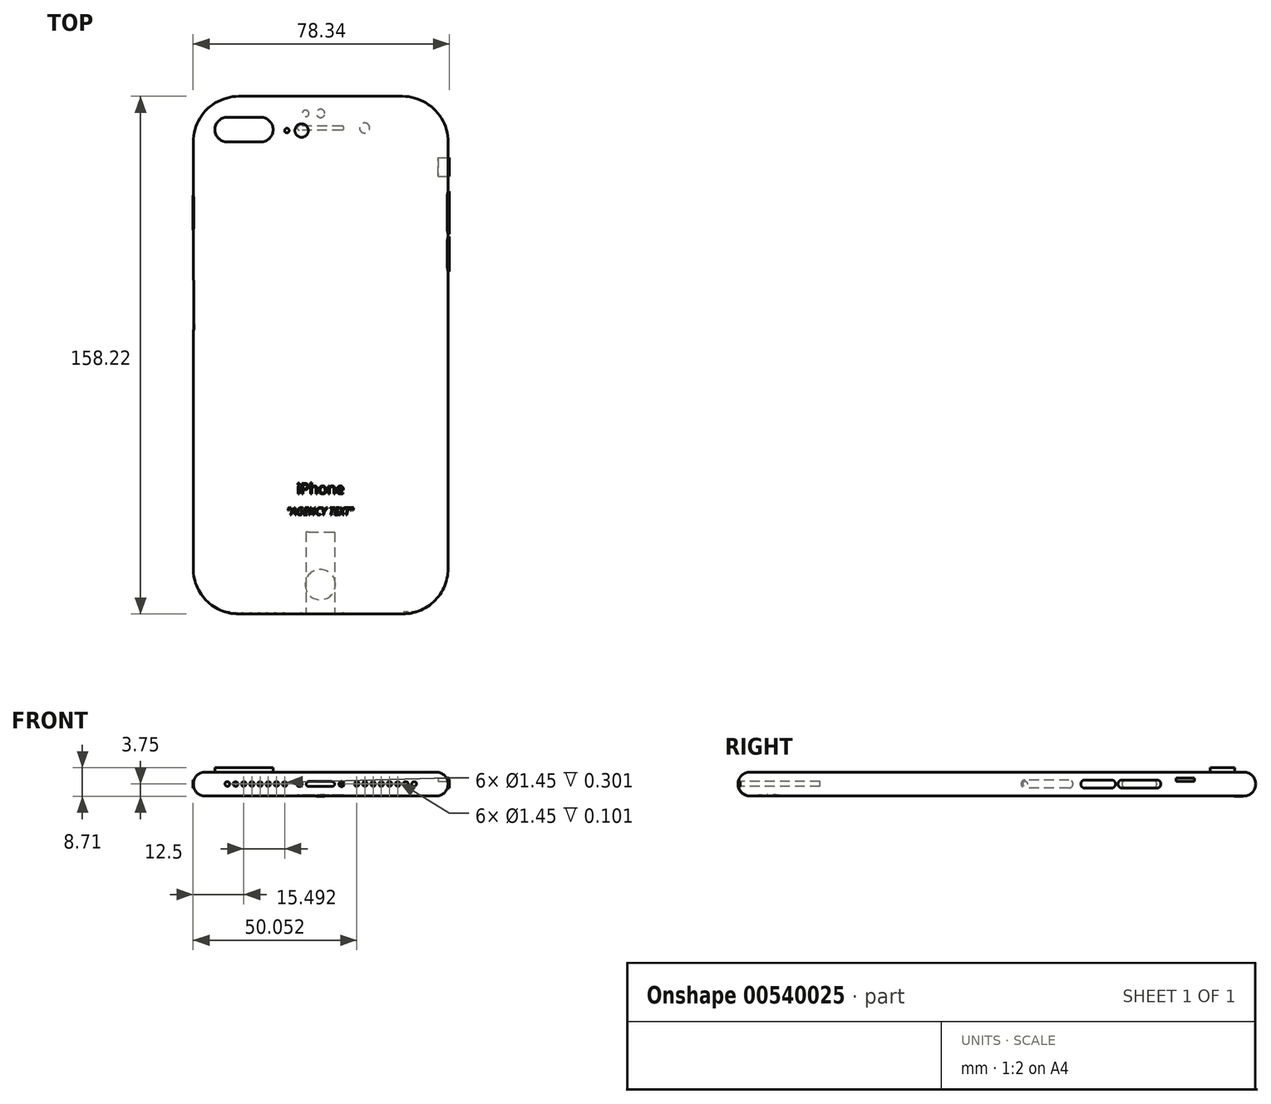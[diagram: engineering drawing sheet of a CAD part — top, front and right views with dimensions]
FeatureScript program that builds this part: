
annotation { "Feature Type Name" : "Feature", "Feature Type Description" : "" }
export const myFeature = defineFeature(function(context is Context, id is Id, definition is map)
    precondition{}
    {
        {
            var Q0;
            Q0=qCreatedBy(makeId("Top.planeOp"),FACE);
            var sketch = newSketch(context, id + "F0", { "sketchPlane" : qUnion([Q0])});
            skLineSegment(sketch, "E0.bottom", {"start": v(-14.7, 124.28) * mm, "end": v(35.32, 124.28) * mm});
            skLineSegment(sketch, "E0.top", {"start": v(-14.7, -33.94) * mm, "end": v(35.32, -33.94) * mm});
            skLineSegment(sketch, "E0.left", {"start": v(-28.64, 110.34) * mm, "end": v(-28.64, -20) * mm});
            skLineSegment(sketch, "E0.right", {"start": v(49.26, 110.34) * mm, "end": v(49.26, -20) * mm});
            skPoint(sketch, "E1.visualSharp", {"position": v(49.26, -33.94) * mm});
            skArc(sketch, "E1.filletArc", {"start": v(35.32, -33.94) * mm, "mid": v(45.18, -29.86) * mm, "end": v(49.26, -20) * mm});
            skPoint(sketch, "E2.visualSharp", {"position": v(-28.64, -33.94) * mm});
            skArc(sketch, "E2.filletArc", {"start": v(-28.64, -20) * mm, "mid": v(-24.55, -29.86) * mm, "end": v(-14.7, -33.94) * mm});
            skPoint(sketch, "E3.visualSharp", {"position": v(49.26, 124.28) * mm});
            skArc(sketch, "E3.filletArc", {"start": v(49.26, 110.34) * mm, "mid": v(45.18, 120.2) * mm, "end": v(35.32, 124.28) * mm});
            skPoint(sketch, "E4.visualSharp", {"position": v(-28.64, 124.28) * mm});
            skArc(sketch, "E4.filletArc", {"start": v(-14.7, 124.28) * mm, "mid": v(-24.55, 120.2) * mm, "end": v(-28.64, 110.34) * mm});
            skSolve(sketch);
        }
        {
            var Q0;
            Q0 = qSketchRegion(id + "F0", true);
            extrude(context, id + "F1", {"entities" : qUnion([Q0]), "depth" : 7.3 * mm, "offsetDistance" : 25 * mm});
        }
        {
            var Q0;
            Q0=makeQuery(id+"F1.opExtrude","CAP_EDGE",EDGE,{"disambiguationData":[OSD([sQuery(id+"F0.wireOp",EDGE,"E0.right")])],"isStart":true});
            fillet(context, id + "F2", {"entities" : qUnion([Q0]), "radius" : 3.65 * mm, "tangentPropagation" : true, "allowEdgeOverflow" : false});
        }
        {
            var Q0;
            Q0=makeQuery(id+"F1.opExtrude","CAP_EDGE",EDGE,{"disambiguationData":[OSD([sQuery(id+"F0.wireOp",EDGE,"E0.right")])],"isStart":false});
            fillet(context, id + "F3", {"entities" : qUnion([Q0]), "radius" : 3.65 * mm, "tangentPropagation" : true, "allowEdgeOverflow" : false});
        }
        {
            var Q0;
            Q0=makeQuery(id+"F1.opExtrude","CAP_FACE",FACE,{"disambiguationData":[OSD([sQuery(id+"F0.wireOp",EDGE,"E0.bottom"),sQuery(id+"F0.wireOp",EDGE,"E0.top"),sQuery(id+"F0.wireOp",EDGE,"E0.left"),sQuery(id+"F0.wireOp",EDGE,"E0.right"),sQuery(id+"F0.wireOp",EDGE,"E1.filletArc"),sQuery(id+"F0.wireOp",EDGE,"E2.filletArc"),sQuery(id+"F0.wireOp",EDGE,"E3.filletArc"),sQuery(id+"F0.wireOp",EDGE,"E4.filletArc")])],"isStart":false});
            var sketch = newSketch(context, id + "F4", { "sketchPlane" : qUnion([Q0])});
            skLineSegment(sketch, "E5.bottom", {"start": v(-14.75, 124.28) * mm, "end": v(35.27, 124.28) * mm});
            skLineSegment(sketch, "E5.top", {"start": v(-14.75, -33.92) * mm, "end": v(35.27, -33.92) * mm});
            skLineSegment(sketch, "E5.left", {"start": v(-28.69, 110.34) * mm, "end": v(-28.69, -19.98) * mm});
            skLineSegment(sketch, "E5.right", {"start": v(49.21, 110.34) * mm, "end": v(49.21, -19.98) * mm});
            skPoint(sketch, "E6.visualSharp", {"position": v(49.21, -33.92) * mm});
            skArc(sketch, "E6.filletArc", {"start": v(35.27, -33.92) * mm, "mid": v(45.13, -29.84) * mm, "end": v(49.21, -19.98) * mm});
            skPoint(sketch, "E7.visualSharp", {"position": v(-28.69, -33.92) * mm});
            skArc(sketch, "E7.filletArc", {"start": v(-28.69, -19.98) * mm, "mid": v(-24.6, -29.84) * mm, "end": v(-14.75, -33.92) * mm});
            skPoint(sketch, "E8.visualSharp", {"position": v(49.21, 124.28) * mm});
            skArc(sketch, "E8.filletArc", {"start": v(49.21, 110.34) * mm, "mid": v(45.13, 120.2) * mm, "end": v(35.27, 124.28) * mm});
            skPoint(sketch, "E9.visualSharp", {"position": v(-28.69, 124.28) * mm});
            skArc(sketch, "E9.filletArc", {"start": v(-14.75, 124.28) * mm, "mid": v(-24.6, 120.2) * mm, "end": v(-28.69, 110.34) * mm});
            skText(sketch, "E10", { "text": "iPhone", "fontName": "OpenSans-Regular.ttf"});
            skText(sketch, "E11", { "text": "\"AGENCY TEXT\"", "fontName": "OpenSans-Italic.ttf"});
            skCircle(sketch, "E12", {"center": v(4.5, 113.8) * mm, "radius": 2.05 * mm});
            skCircle(sketch, "E13", {"center": v(0, 113.8) * mm, "radius": 0.7 * mm});
            skLineSegment(sketch, "E14.bottom", {"start": v(-7.97, 117.88) * mm, "end": v(-18.24, 117.88) * mm});
            skLineSegment(sketch, "E14.top", {"start": v(-7.97, 110.34) * mm, "end": v(-18.24, 110.34) * mm});
            skLineSegment(sketch, "E14.left", {"start": v(-4.2, 114.1) * mm, "end": v(-4.2, 114.1) * mm});
            skLineSegment(sketch, "E14.right", {"start": v(-22, 114.1) * mm, "end": v(-22, 114.1) * mm});
            skPoint(sketch, "E15.visualSharp", {"position": v(-22, 117.88) * mm});
            skArc(sketch, "E15.filletArc", {"start": v(-18.24, 117.88) * mm, "mid": v(-20.9, 116.77) * mm, "end": v(-22, 114.1) * mm});
            skPoint(sketch, "E16.visualSharp", {"position": v(-22, 110.34) * mm});
            skArc(sketch, "E16.filletArc", {"start": v(-22, 114.1) * mm, "mid": v(-20.9, 111.44) * mm, "end": v(-18.24, 110.34) * mm});
            skPoint(sketch, "E17.visualSharp", {"position": v(-4.2, 110.34) * mm});
            skArc(sketch, "E17.filletArc", {"start": v(-7.97, 110.34) * mm, "mid": v(-5.3, 111.44) * mm, "end": v(-4.2, 114.1) * mm});
            skPoint(sketch, "E18.visualSharp", {"position": v(-4.2, 117.88) * mm});
            skArc(sketch, "E18.filletArc", {"start": v(-4.2, 114.1) * mm, "mid": v(-5.3, 116.77) * mm, "end": v(-7.97, 117.88) * mm});
            const initialGuessF4  = {"E10": [0.003, 0.00278, 1, 0, 0.00322], "E11": [0, -0.00364, 1, 0, 0.00222]};
            skSetInitialGuess(sketch, initialGuessF4);
            skSolve(sketch);
        }
        {
            var Q0;
            Q0=makeQuery(id+"F4.imprint","IMPRINT",FACE,{"disambiguationData":[TD([[makeQuery(id+"F4.imprint","IMPRINT",EDGE,{"derivedFrom":sQuery(id+"F4.wireOp",EDGE,"E10.sketch_text.stroke-79")}),-1.0]])]});
            var Q1;
            Q1=makeQuery(id+"F4.imprint","IMPRINT",FACE,{"disambiguationData":[TD([[makeQuery(id+"F4.imprint","IMPRINT",EDGE,{"derivedFrom":sQuery(id+"F4.wireOp",EDGE,"E10.sketch_text.stroke-62")}),-1.0]])]});
            var Q2;
            Q2=makeQuery(id+"F4.imprint","IMPRINT",FACE,{"disambiguationData":[TD([[makeQuery(id+"F4.imprint","IMPRINT",EDGE,{"derivedFrom":sQuery(id+"F4.wireOp",EDGE,"E10.sketch_text.stroke-45")}),-1.0]])]});
            var Q3;
            Q3=makeQuery(id+"F4.imprint","IMPRINT",FACE,{"disambiguationData":[TD([[makeQuery(id+"F4.imprint","IMPRINT",EDGE,{"derivedFrom":sQuery(id+"F4.wireOp",EDGE,"E10.sketch_text.stroke-27")}),-1.0]])]});
            var Q4;
            Q4=makeQuery(id+"F4.imprint","IMPRINT",FACE,{"disambiguationData":[TD([[makeQuery(id+"F4.imprint","IMPRINT",EDGE,{"derivedFrom":sQuery(id+"F4.wireOp",EDGE,"E10.sketch_text.stroke-12")}),-1.0]])]});
            var Q5;
            Q5=makeQuery(id+"F4.imprint","IMPRINT",FACE,{"disambiguationData":[TD([[makeQuery(id+"F4.imprint","IMPRINT",EDGE,{"derivedFrom":sQuery(id+"F4.wireOp",EDGE,"E10.sketch_text.stroke-0")}),-1.0]])]});
            var Q6;
            Q6=makeQuery(id+"F4.imprint","IMPRINT",FACE,{"disambiguationData":[TD([[makeQuery(id+"F4.imprint","IMPRINT",EDGE,{"derivedFrom":sQuery(id+"F4.wireOp",EDGE,"E10.sketch_text.stroke-4")}),-1.0]])]});
            extrude(context, id + "F5", {"entities" : qUnion([Q0, Q1, Q2, Q3, Q4, Q5, Q6]), "operationType" : NewBodyOperationType.REMOVE, "oppositeDirection" : true, "depth" : .1 * mm, "offsetDistance" : 25 * mm});
        }
        {
            var Q0;
            Q0=makeQuery(id+"F4.imprint","IMPRINT",FACE,{"disambiguationData":[TD([[makeQuery(id+"F4.imprint","IMPRINT",EDGE,{"derivedFrom":sQuery(id+"F4.wireOp",EDGE,"E11.sketch_text.stroke-8")}),-1.0]])]});
            var Q1;
            Q1=makeQuery(id+"F4.imprint","IMPRINT",FACE,{"disambiguationData":[TD([[makeQuery(id+"F4.imprint","IMPRINT",EDGE,{"derivedFrom":sQuery(id+"F4.wireOp",EDGE,"E11.sketch_text.stroke-4")}),-1.0]])]});
            var Q2;
            Q2=makeQuery(id+"F4.imprint","IMPRINT",FACE,{"disambiguationData":[TD([[makeQuery(id+"F4.imprint","IMPRINT",EDGE,{"derivedFrom":sQuery(id+"F4.wireOp",EDGE,"E11.sketch_text.stroke-0")}),-1.0]])]});
            var Q3;
            Q3=makeQuery(id+"F4.imprint","IMPRINT",FACE,{"disambiguationData":[TD([[makeQuery(id+"F4.imprint","IMPRINT",EDGE,{"derivedFrom":sQuery(id+"F4.wireOp",EDGE,"E11.sketch_text.stroke-21")}),-1.0]])]});
            var Q4;
            Q4=makeQuery(id+"F4.imprint","IMPRINT",FACE,{"disambiguationData":[TD([[makeQuery(id+"F4.imprint","IMPRINT",EDGE,{"derivedFrom":sQuery(id+"F4.wireOp",EDGE,"E11.sketch_text.stroke-43")}),-1.0]])]});
            var Q5;
            Q5=makeQuery(id+"F4.imprint","IMPRINT",FACE,{"disambiguationData":[TD([[makeQuery(id+"F4.imprint","IMPRINT",EDGE,{"derivedFrom":sQuery(id+"F4.wireOp",EDGE,"E11.sketch_text.stroke-55")}),-1.0]])]});
            var Q6;
            Q6=makeQuery(id+"F4.imprint","IMPRINT",FACE,{"disambiguationData":[TD([[makeQuery(id+"F4.imprint","IMPRINT",EDGE,{"derivedFrom":sQuery(id+"F4.wireOp",EDGE,"E11.sketch_text.stroke-69")}),-1.0]])]});
            var Q7;
            Q7=makeQuery(id+"F4.imprint","IMPRINT",FACE,{"disambiguationData":[TD([[makeQuery(id+"F4.imprint","IMPRINT",EDGE,{"derivedFrom":sQuery(id+"F4.wireOp",EDGE,"E11.sketch_text.stroke-86")}),-1.0]])]});
            extrude(context, id + "F6", {"entities" : qUnion([Q0, Q1, Q2, Q3, Q4, Q5, Q6, Q7]), "operationType" : NewBodyOperationType.REMOVE, "oppositeDirection" : true, "depth" : .1 * mm, "offsetDistance" : 25 * mm});
        }
        {
            var Q0;
            Q0=makeQuery(id+"F4.imprint","IMPRINT",FACE,{"disambiguationData":[TD([[makeQuery(id+"F4.imprint","IMPRINT",EDGE,{"derivedFrom":sQuery(id+"F4.wireOp",EDGE,"E11.sketch_text.stroke-95")}),-1.0]])]});
            var Q1;
            Q1=makeQuery(id+"F4.imprint","IMPRINT",FACE,{"disambiguationData":[TD([[makeQuery(id+"F4.imprint","IMPRINT",EDGE,{"derivedFrom":sQuery(id+"F4.wireOp",EDGE,"E11.sketch_text.stroke-103")}),-1.0]])]});
            var Q2;
            Q2=makeQuery(id+"F4.imprint","IMPRINT",FACE,{"disambiguationData":[TD([[makeQuery(id+"F4.imprint","IMPRINT",EDGE,{"derivedFrom":sQuery(id+"F4.wireOp",EDGE,"E11.sketch_text.stroke-115")}),-1.0]])]});
            var Q3;
            Q3=makeQuery(id+"F4.imprint","IMPRINT",FACE,{"disambiguationData":[TD([[makeQuery(id+"F4.imprint","IMPRINT",EDGE,{"derivedFrom":sQuery(id+"F4.wireOp",EDGE,"E11.sketch_text.stroke-127")}),-1.0]])]});
            var Q4;
            Q4=makeQuery(id+"F4.imprint","IMPRINT",FACE,{"disambiguationData":[TD([[makeQuery(id+"F4.imprint","IMPRINT",EDGE,{"derivedFrom":sQuery(id+"F4.wireOp",EDGE,"E11.sketch_text.stroke-135")}),-1.0]])]});
            var Q5;
            Q5=makeQuery(id+"F4.imprint","IMPRINT",FACE,{"disambiguationData":[TD([[makeQuery(id+"F4.imprint","IMPRINT",EDGE,{"derivedFrom":sQuery(id+"F4.wireOp",EDGE,"E11.sketch_text.stroke-139")}),-1.0]])]});
            extrude(context, id + "F7", {"entities" : qUnion([Q0, Q1, Q2, Q3, Q4, Q5]), "operationType" : NewBodyOperationType.REMOVE, "oppositeDirection" : true, "depth" : .1 * mm, "offsetDistance" : 25 * mm});
        }
        {
            var Q0;
            Q0=makeQuery(id+"F4.imprint","IMPRINT",FACE,{"disambiguationData":[TD([[makeQuery(id+"F4.imprint","IMPRINT",EDGE,{"derivedFrom":sQuery(id+"F4.wireOp",EDGE,"E14.bottom")}),1.0]])]});
            extrude(context, id + "F8", {"entities" : qUnion([Q0]), "operationType" : NewBodyOperationType.ADD, "depth" : 1.31 * mm, "offsetDistance" : 25 * mm});
        }
        {
            var Q0;
            Q0=sQuery(id+"F0.wireOp",EDGE,"E0.top");
            cPlane(context, id + "F9", {"entities" : qUnion([Q0]), "cplaneType" : CPlaneType.LINE_ANGLE, "offset" : 25 * mm, "angle" : 0 * degree, "width" : 150 * mm, "height" : 150 * mm});
        }
        {
            var Q0;
            Q0=qCreatedBy(id+"F9.planeOp",FACE);
            var sketch = newSketch(context, id + "F10", { "sketchPlane" : qUnion([Q0])});
            skCircle(sketch, "E19", {"center": v(10.7, 3.65) * mm, "radius": 0.72 * mm});
            skCircle(sketch, "E20", {"center": v(3.2, 3.65) * mm, "radius": 0.72 * mm});
            skCircle(sketch, "E21", {"center": v(18.2, 3.65) * mm, "radius": 0.72 * mm});
            skCircle(sketch, "E22", {"center": v(15.7, 3.65) * mm, "radius": 0.72 * mm});
            skCircle(sketch, "E23", {"center": v(13.2, 3.65) * mm, "radius": 0.72 * mm});
            skCircle(sketch, "E24", {"center": v(8.2, 3.65) * mm, "radius": 0.72 * mm});
            skCircle(sketch, "E25", {"center": v(5.7, 3.65) * mm, "radius": 0.72 * mm});
            skCircle(sketch, "E26", {"center": v(-3.84, 3.65) * mm, "radius": 0.8 * mm});
            skLineSegment(sketch, "E27.bottom", {"start": v(-6.64, 2.9) * mm, "end": v(-13.84, 2.9) * mm});
            skLineSegment(sketch, "E27.top", {"start": v(-6.64, 4.4) * mm, "end": v(-13.84, 4.4) * mm});
            skLineSegment(sketch, "E27.left", {"start": v(-5.89, 3.65) * mm, "end": v(-5.89, 3.65) * mm});
            skLineSegment(sketch, "E27.right", {"start": v(-14.59, 3.65) * mm, "end": v(-14.59, 3.65) * mm});
            skPoint(sketch, "E28.visualSharp", {"position": v(-5.89, 4.4) * mm});
            skArc(sketch, "E28.filletArc", {"start": v(-5.89, 3.65) * mm, "mid": v(-6.1, 4.18) * mm, "end": v(-6.64, 4.4) * mm});
            skPoint(sketch, "E29.visualSharp", {"position": v(-5.89, 2.9) * mm});
            skArc(sketch, "E29.filletArc", {"start": v(-6.64, 2.9) * mm, "mid": v(-6.1, 3.12) * mm, "end": v(-5.89, 3.65) * mm});
            skPoint(sketch, "E30.visualSharp", {"position": v(-14.59, 2.9) * mm});
            skArc(sketch, "E30.filletArc", {"start": v(-14.59, 3.65) * mm, "mid": v(-14.37, 3.12) * mm, "end": v(-13.84, 2.9) * mm});
            skPoint(sketch, "E31.visualSharp", {"position": v(-14.59, 4.4) * mm});
            skArc(sketch, "E31.filletArc", {"start": v(-13.84, 4.4) * mm, "mid": v(-14.37, 4.18) * mm, "end": v(-14.59, 3.65) * mm});
            skLineSegment(sketch, "E32", {"start": v(-3.12, 4) * mm, "end": v(-4.2, 2.93) * mm});
            skLineSegment(sketch, "E33", {"start": v(-3.5, 4.37) * mm, "end": v(-4.56, 3.3) * mm});
            skCircle(sketch, "E34", {"center": v(0.7, 3.65) * mm, "radius": 0.72 * mm});
            skCircle(sketch, "E35", {"center": v(-21.36, 3.65) * mm, "radius": 0.72 * mm});
            skCircle(sketch, "E36", {"center": v(-23.86, 3.65) * mm, "radius": 0.72 * mm});
            skCircle(sketch, "E37", {"center": v(-26.36, 3.65) * mm, "radius": 0.72 * mm});
            skCircle(sketch, "E38", {"center": v(-28.86, 3.65) * mm, "radius": 0.72 * mm});
            skCircle(sketch, "E39", {"center": v(-31.36, 3.65) * mm, "radius": 0.72 * mm});
            skCircle(sketch, "E40", {"center": v(-33.86, 3.65) * mm, "radius": 0.72 * mm});
            skCircle(sketch, "E41", {"center": v(-36.36, 3.65) * mm, "radius": 0.72 * mm});
            skCircle(sketch, "E42", {"center": v(-38.86, 3.65) * mm, "radius": 0.72 * mm});
            skSolve(sketch);
        }
        {
            var Q0;
            Q0=makeQuery(id+"F10.imprint","IMPRINT",FACE,{"disambiguationData":[TD([[makeQuery(id+"F10.imprint","IMPRINT",EDGE,{"derivedFrom":sQuery(id+"F10.wireOp",EDGE,"E27.bottom")}),-1.0]])]});
            extrude(context, id + "F11", {"entities" : qUnion([Q0]), "operationType" : NewBodyOperationType.REMOVE, "depth" : 25 * mm, "offsetDistance" : 25 * mm});
        }
        {
            var Q0;
            {var subQ0=sQuery(id+"F10.wireOp",EDGE,"E32");Q0=makeQuery(id+"F10.imprint","IMPRINT",FACE,{"disambiguationData":[TD([[makeQuery(id+"F10.imprint","IMPRINT",EDGE,{"derivedFrom":subQ0}),1.0]])]});}
            var Q1;
            {var subQ0=sQuery(id+"F10.wireOp",EDGE,"E33");Q1=makeQuery(id+"F10.imprint","IMPRINT",FACE,{"disambiguationData":[TD([[makeQuery(id+"F10.imprint","IMPRINT",EDGE,{"derivedFrom":subQ0}),-1.0]])]});}
            extrude(context, id + "F12", {"entities" : qUnion([Q0, Q1]), "operationType" : NewBodyOperationType.REMOVE, "depth" : .1 * mm, "offsetDistance" : 25 * mm});
        }
        {
            var Q0;
            {var subQ0=sQuery(id+"F10.wireOp",EDGE,"E32");Q0=makeQuery(id+"F10.imprint","IMPRINT",FACE,{"disambiguationData":[TD([[makeQuery(id+"F10.imprint","IMPRINT",EDGE,{"derivedFrom":subQ0}),-1.0]])]});}
            extrude(context, id + "F13", {"entities" : qUnion([Q0]), "operationType" : NewBodyOperationType.REMOVE, "depth" : .3 * mm, "offsetDistance" : 25 * mm});
        }
        {
            var Q0;
            Q0=qCreatedBy(id+"F9.planeOp",FACE);
            var sketch = newSketch(context, id + "F14", { "sketchPlane" : qUnion([Q0])});
            skCircle(sketch, "E43", {"center": v(-5.48, -0.16) * mm, "radius": 0.72 * mm});
            skCircle(sketch, "E44", {"center": v(-5.68, -0.16) * mm, "radius": 0.72 * mm});
            skCircle(sketch, "E45", {"center": v(7.87, -0.08) * mm, "radius": 0.72 * mm});
            skCircle(sketch, "E46", {"center": v(-5.06, -0.1) * mm, "radius": 0.72 * mm});
            skCircle(sketch, "E47", {"center": v(-5.93, -0.07) * mm, "radius": 0.72 * mm});
            skCircle(sketch, "E48", {"center": v(-6.16, -0.04) * mm, "radius": 0.72 * mm});
            skCircle(sketch, "E49", {"center": v(-6.37, 0.03) * mm, "radius": 0.72 * mm});
            skCircle(sketch, "E50", {"center": v(-16.7, 3.65) * mm, "radius": 0.8 * mm});
            skLineSegment(sketch, "E51", {"start": v(-16, 4.06) * mm, "end": v(-16.86, 2.87) * mm});
            skLineSegment(sketch, "E52", {"start": v(-16.57, 4.44) * mm, "end": v(-17.4, 3.29) * mm});
            skSolve(sketch);
        }
        {
            var Q0;
            {var subQ0=sQuery(id+"F14.wireOp",EDGE,"E51");Q0=makeQuery(id+"F14.imprint","IMPRINT",FACE,{"disambiguationData":[TD([[makeQuery(id+"F14.imprint","IMPRINT",EDGE,{"derivedFrom":subQ0}),1.0]])]});}
            var Q1;
            {var subQ0=sQuery(id+"F14.wireOp",EDGE,"E52");Q1=makeQuery(id+"F14.imprint","IMPRINT",FACE,{"disambiguationData":[TD([[makeQuery(id+"F14.imprint","IMPRINT",EDGE,{"derivedFrom":subQ0}),-1.0]])]});}
            extrude(context, id + "F15", {"entities" : qUnion([Q0, Q1]), "operationType" : NewBodyOperationType.REMOVE, "depth" : .1 * mm, "offsetDistance" : 25 * mm});
        }
        {
            var Q0;
            {var subQ0=sQuery(id+"F14.wireOp",EDGE,"E51");Q0=makeQuery(id+"F14.imprint","IMPRINT",FACE,{"disambiguationData":[TD([[makeQuery(id+"F14.imprint","IMPRINT",EDGE,{"derivedFrom":subQ0}),-1.0]])]});}
            extrude(context, id + "F16", {"entities" : qUnion([Q0]), "operationType" : NewBodyOperationType.REMOVE, "depth" : .3 * mm, "offsetDistance" : 25 * mm});
        }
        {
            var Q0;
            Q0=makeQuery(id+"F10.imprint","IMPRINT",FACE,{"disambiguationData":[TD([[makeQuery(id+"F10.imprint","IMPRINT",EDGE,{"derivedFrom":sQuery(id+"F10.wireOp",EDGE,"E21")}),1.0]])]});
            var Q1;
            Q1=makeQuery(id+"F10.imprint","IMPRINT",FACE,{"disambiguationData":[TD([[makeQuery(id+"F10.imprint","IMPRINT",EDGE,{"derivedFrom":sQuery(id+"F10.wireOp",EDGE,"E22")}),1.0]])]});
            var Q2;
            Q2=makeQuery(id+"F10.imprint","IMPRINT",FACE,{"disambiguationData":[TD([[makeQuery(id+"F10.imprint","IMPRINT",EDGE,{"derivedFrom":sQuery(id+"F10.wireOp",EDGE,"E23")}),1.0]])]});
            var Q3;
            Q3=makeQuery(id+"F10.imprint","IMPRINT",FACE,{"disambiguationData":[TD([[makeQuery(id+"F10.imprint","IMPRINT",EDGE,{"derivedFrom":sQuery(id+"F10.wireOp",EDGE,"E19")}),1.0]])]});
            var Q4;
            Q4=makeQuery(id+"F10.imprint","IMPRINT",FACE,{"disambiguationData":[TD([[makeQuery(id+"F10.imprint","IMPRINT",EDGE,{"derivedFrom":sQuery(id+"F10.wireOp",EDGE,"E24")}),1.0]])]});
            var Q5;
            Q5=makeQuery(id+"F10.imprint","IMPRINT",FACE,{"disambiguationData":[TD([[makeQuery(id+"F10.imprint","IMPRINT",EDGE,{"derivedFrom":sQuery(id+"F10.wireOp",EDGE,"E25")}),1.0]])]});
            var Q6;
            Q6=makeQuery(id+"F10.imprint","IMPRINT",FACE,{"disambiguationData":[TD([[makeQuery(id+"F10.imprint","IMPRINT",EDGE,{"derivedFrom":sQuery(id+"F10.wireOp",EDGE,"E20")}),1.0]])]});
            extrude(context, id + "F17", {"entities" : qUnion([Q0, Q1, Q2, Q3, Q4, Q5, Q6]), "operationType" : NewBodyOperationType.REMOVE, "depth" : .3 * mm, "offsetDistance" : 25 * mm});
        }
        {
            var Q0;
            Q0=makeQuery(id+"F10.imprint","IMPRINT",FACE,{"disambiguationData":[TD([[makeQuery(id+"F10.imprint","IMPRINT",EDGE,{"derivedFrom":sQuery(id+"F10.wireOp",EDGE,"E21")}),1.0]])]});
            extrude(context, id + "F18", {"entities" : qUnion([Q0]), "operationType" : NewBodyOperationType.REMOVE, "depth" : .7 * mm, "offsetDistance" : 25 * mm});
        }
        {
            var Q0;
            Q0=makeQuery(id+"F10.imprint","IMPRINT",FACE,{"disambiguationData":[TD([[makeQuery(id+"F10.imprint","IMPRINT",EDGE,{"derivedFrom":sQuery(id+"F10.wireOp",EDGE,"E34")}),1.0]])]});
            extrude(context, id + "F19", {"entities" : qUnion([Q0]), "operationType" : NewBodyOperationType.REMOVE, "depth" : .3 * mm, "offsetDistance" : 25 * mm});
        }
        {
            var Q0;
            Q0=makeQuery(id+"F10.imprint","IMPRINT",FACE,{"disambiguationData":[TD([[makeQuery(id+"F10.imprint","IMPRINT",EDGE,{"derivedFrom":sQuery(id+"F10.wireOp",EDGE,"E35")}),1.0]])]});
            var Q1;
            Q1=makeQuery(id+"F10.imprint","IMPRINT",FACE,{"disambiguationData":[TD([[makeQuery(id+"F10.imprint","IMPRINT",EDGE,{"derivedFrom":sQuery(id+"F10.wireOp",EDGE,"E36")}),1.0]])]});
            var Q2;
            Q2=makeQuery(id+"F10.imprint","IMPRINT",FACE,{"disambiguationData":[TD([[makeQuery(id+"F10.imprint","IMPRINT",EDGE,{"derivedFrom":sQuery(id+"F10.wireOp",EDGE,"E37")}),1.0]])]});
            var Q3;
            Q3=makeQuery(id+"F10.imprint","IMPRINT",FACE,{"disambiguationData":[TD([[makeQuery(id+"F10.imprint","IMPRINT",EDGE,{"derivedFrom":sQuery(id+"F10.wireOp",EDGE,"E38")}),1.0]])]});
            var Q4;
            Q4=makeQuery(id+"F10.imprint","IMPRINT",FACE,{"disambiguationData":[TD([[makeQuery(id+"F10.imprint","IMPRINT",EDGE,{"derivedFrom":sQuery(id+"F10.wireOp",EDGE,"E39")}),1.0]])]});
            var Q5;
            Q5=makeQuery(id+"F10.imprint","IMPRINT",FACE,{"disambiguationData":[TD([[makeQuery(id+"F10.imprint","IMPRINT",EDGE,{"derivedFrom":sQuery(id+"F10.wireOp",EDGE,"E40")}),1.0]])]});
            var Q6;
            Q6=makeQuery(id+"F10.imprint","IMPRINT",FACE,{"disambiguationData":[TD([[makeQuery(id+"F10.imprint","IMPRINT",EDGE,{"derivedFrom":sQuery(id+"F10.wireOp",EDGE,"E41")}),1.0]])]});
            extrude(context, id + "F20", {"entities" : qUnion([Q0, Q1, Q2, Q3, Q4, Q5, Q6]), "operationType" : NewBodyOperationType.REMOVE, "depth" : .1 * mm, "offsetDistance" : 25 * mm});
        }
        {
            var Q0;
            Q0=makeQuery(id+"F10.imprint","IMPRINT",FACE,{"disambiguationData":[TD([[makeQuery(id+"F10.imprint","IMPRINT",EDGE,{"derivedFrom":sQuery(id+"F10.wireOp",EDGE,"E41")}),1.0]])]});
            extrude(context, id + "F21", {"entities" : qUnion([Q0]), "operationType" : NewBodyOperationType.REMOVE, "depth" : .7 * mm, "offsetDistance" : 25 * mm});
        }
        {
            var Q0;
            Q0=makeQuery(id+"F10.imprint","IMPRINT",FACE,{"disambiguationData":[TD([[makeQuery(id+"F10.imprint","IMPRINT",EDGE,{"derivedFrom":sQuery(id+"F10.wireOp",EDGE,"E42")}),1.0]])]});
            extrude(context, id + "F22", {"entities" : qUnion([Q0]), "operationType" : NewBodyOperationType.REMOVE, "depth" : .7 * mm, "offsetDistance" : 25 * mm});
        }
        {
            var Q0;
            Q0=makeQuery(id+"F0.imprint","IMPRINT",FACE,{"disambiguationData":[TD([[makeQuery(id+"F0.imprint","IMPRINT",EDGE,{"derivedFrom":sQuery(id+"F0.wireOp",EDGE,"E0.bottom")}),-1.0]])]});
            var sketch = newSketch(context, id + "F23", { "sketchPlane" : qUnion([Q0])});
            skCircle(sketch, "E53", {"center": v(10.22, -24.97) * mm, "radius": 4.64 * mm});
            skCircle(sketch, "E54", {"center": v(23.73, 114.62) * mm, "radius": 1.55 * mm});
            skCircle(sketch, "E55", {"center": v(10.3, 119.06) * mm, "radius": 1.29 * mm});
            skCircle(sketch, "E56", {"center": v(5.71, 119.06) * mm, "radius": 1 * mm});
            skLineSegment(sketch, "E57.bottom", {"start": v(16.85, 115.18) * mm, "end": v(3.74, 115.18) * mm});
            skLineSegment(sketch, "E57.top", {"start": v(16.83, 113.98) * mm, "end": v(3.76, 113.98) * mm});
            skLineSegment(sketch, "E57.left", {"start": v(17.43, 114.6) * mm, "end": v(17.43, 114.58) * mm});
            skLineSegment(sketch, "E57.right", {"start": v(3.16, 114.6) * mm, "end": v(3.16, 114.58) * mm});
            skPoint(sketch, "E58.visualSharp", {"position": v(17.43, 115.18) * mm});
            skArc(sketch, "E58.filletArc", {"start": v(17.43, 114.6) * mm, "mid": v(17.26, 115) * mm, "end": v(16.85, 115.18) * mm});
            skPoint(sketch, "E59.visualSharp", {"position": v(17.43, 113.98) * mm});
            skArc(sketch, "E59.filletArc", {"start": v(16.83, 113.98) * mm, "mid": v(17.26, 114.15) * mm, "end": v(17.43, 114.58) * mm});
            skPoint(sketch, "E60.visualSharp", {"position": v(3.16, 113.98) * mm});
            skArc(sketch, "E60.filletArc", {"start": v(3.16, 114.58) * mm, "mid": v(3.34, 114.15) * mm, "end": v(3.76, 113.98) * mm});
            skPoint(sketch, "E61.visualSharp", {"position": v(3.16, 115.18) * mm});
            skArc(sketch, "E61.filletArc", {"start": v(3.74, 115.18) * mm, "mid": v(3.33, 115) * mm, "end": v(3.16, 114.6) * mm});
            skSolve(sketch);
        }
        {
            var Q0;
            Q0=makeQuery(id+"F23.imprint","IMPRINT",FACE,{"disambiguationData":[TD([[makeQuery(id+"F23.imprint","IMPRINT",EDGE,{"derivedFrom":sQuery(id+"F23.wireOp",EDGE,"E54")}),1.0]])]});
            extrude(context, id + "F24", {"entities" : qUnion([Q0]), "operationType" : NewBodyOperationType.REMOVE, "depth" : .1 * mm, "offsetDistance" : 25 * mm});
        }
        {
            var Q0;
            Q0=makeQuery(id+"F23.imprint","IMPRINT",FACE,{"disambiguationData":[TD([[makeQuery(id+"F23.imprint","IMPRINT",EDGE,{"derivedFrom":sQuery(id+"F23.wireOp",EDGE,"E55")}),1.0]])]});
            extrude(context, id + "F25", {"entities" : qUnion([Q0]), "operationType" : NewBodyOperationType.ADD, "oppositeDirection" : true, "depth" : .1 * mm, "offsetDistance" : 25 * mm});
        }
        {
            var Q0;
            Q0=makeQuery(id+"F23.imprint","IMPRINT",FACE,{"disambiguationData":[TD([[makeQuery(id+"F23.imprint","IMPRINT",EDGE,{"derivedFrom":sQuery(id+"F23.wireOp",EDGE,"E54")}),1.0]])]});
            extrude(context, id + "F26", {"entities" : qUnion([Q0]), "operationType" : NewBodyOperationType.REMOVE, "oppositeDirection" : true, "depth" : .1 * mm, "offsetDistance" : 25 * mm});
        }
        {
            var Q0;
            Q0=makeQuery(id+"F23.imprint","IMPRINT",FACE,{"disambiguationData":[TD([[makeQuery(id+"F23.imprint","IMPRINT",EDGE,{"derivedFrom":sQuery(id+"F23.wireOp",EDGE,"E56")}),1.0]])]});
            extrude(context, id + "F27", {"entities" : qUnion([Q0]), "operationType" : NewBodyOperationType.REMOVE, "depth" : .1 * mm, "offsetDistance" : 25 * mm});
        }
        {
            var Q0;
            Q0=makeQuery(id+"F23.imprint","IMPRINT",FACE,{"disambiguationData":[TD([[makeQuery(id+"F23.imprint","IMPRINT",EDGE,{"derivedFrom":sQuery(id+"F23.wireOp",EDGE,"E57.bottom")}),1.0]])]});
            extrude(context, id + "F28", {"entities" : qUnion([Q0]), "operationType" : NewBodyOperationType.REMOVE, "depth" : .3 * mm, "offsetDistance" : 25 * mm});
        }
        {
            var Q0;
            Q0=makeQuery(id+"F23.imprint","IMPRINT",FACE,{"disambiguationData":[TD([[makeQuery(id+"F23.imprint","IMPRINT",EDGE,{"derivedFrom":sQuery(id+"F23.wireOp",EDGE,"E53")}),1.0]])]});
            extrude(context, id + "F29", {"entities" : qUnion([Q0]), "operationType" : NewBodyOperationType.REMOVE, "depth" : .5 * mm, "offsetDistance" : 25 * mm});
        }
        {
            var Q0;
            Q0=makeQuery(id+"F4.imprint","IMPRINT",FACE,{"disambiguationData":[TD([[makeQuery(id+"F4.imprint","IMPRINT",EDGE,{"derivedFrom":sQuery(id+"F4.wireOp",EDGE,"E12")}),1.0]])]});
            extrude(context, id + "F30", {"entities" : qUnion([Q0]), "operationType" : NewBodyOperationType.REMOVE, "oppositeDirection" : true, "depth" : .1 * mm, "offsetDistance" : 25 * mm});
        }
        {
            var Q0;
            Q0=makeQuery(id+"F4.imprint","IMPRINT",FACE,{"disambiguationData":[TD([[makeQuery(id+"F4.imprint","IMPRINT",EDGE,{"derivedFrom":sQuery(id+"F4.wireOp",EDGE,"E13")}),1.0]])]});
            extrude(context, id + "F31", {"entities" : qUnion([Q0]), "operationType" : NewBodyOperationType.REMOVE, "oppositeDirection" : true, "depth" : .1 * mm, "offsetDistance" : 25 * mm});
        }
        {
            var Q0;
            Q0=sQuery(id+"F4.wireOp",EDGE,"E5.right");
            var Q1;
            Q1=sQuery(id+"F0.wireOp",EDGE,"E0.right");
            cPlane(context, id + "F32", {"entities" : qUnion([Q0, Q1]), "cplaneType" : CPlaneType.LINE_ANGLE, "offset" : 25 * mm, "angle" : 0 * degree, "width" : 150 * mm, "height" : 150 * mm});
        }
        {
            var Q0;
            Q0=qCreatedBy(id+"F32.planeOp",FACE);
            var sketch = newSketch(context, id + "F33", { "sketchPlane" : qUnion([Q0])});
            skLineSegment(sketch, "E62.bottom", {"start": v(105.5, 5.16) * mm, "end": v(99.89, 5.16) * mm});
            skLineSegment(sketch, "E62.top", {"start": v(105.5, 3.19) * mm, "end": v(99.89, 3.19) * mm});
            skLineSegment(sketch, "E62.left", {"start": v(105.5, 5.16) * mm, "end": v(105.5, 3.19) * mm});
            skLineSegment(sketch, "E62.right", {"start": v(99.89, 5.16) * mm, "end": v(99.89, 3.19) * mm});
            skLineSegment(sketch, "E63.bottom", {"start": v(94.04, 4.55) * mm, "end": v(83.42, 4.55) * mm});
            skLineSegment(sketch, "E63.top", {"start": v(94.04, 2.07) * mm, "end": v(83.42, 2.07) * mm});
            skLineSegment(sketch, "E63.left", {"start": v(95.28, 3.31) * mm, "end": v(95.28, 3.31) * mm});
            skLineSegment(sketch, "E63.right", {"start": v(82.18, 3.31) * mm, "end": v(82.18, 3.31) * mm});
            skLineSegment(sketch, "E64.bottom", {"start": v(80.19, 4.55) * mm, "end": v(72.05, 4.55) * mm});
            skLineSegment(sketch, "E64.top", {"start": v(80.19, 2.07) * mm, "end": v(72.05, 2.07) * mm});
            skLineSegment(sketch, "E64.left", {"start": v(81.43, 3.31) * mm, "end": v(81.43, 3.31) * mm});
            skLineSegment(sketch, "E64.right", {"start": v(70.8, 3.31) * mm, "end": v(70.8, 3.31) * mm});
            skPoint(sketch, "E65.visualSharp", {"position": v(70.8, 4.55) * mm});
            skArc(sketch, "E65.filletArc", {"start": v(72.05, 4.55) * mm, "mid": v(71.17, 4.19) * mm, "end": v(70.8, 3.31) * mm});
            skPoint(sketch, "E66.visualSharp", {"position": v(70.8, 2.07) * mm});
            skArc(sketch, "E66.filletArc", {"start": v(70.8, 3.31) * mm, "mid": v(71.17, 2.44) * mm, "end": v(72.05, 2.07) * mm});
            skPoint(sketch, "E67.visualSharp", {"position": v(81.43, 2.07) * mm});
            skArc(sketch, "E67.filletArc", {"start": v(80.19, 2.07) * mm, "mid": v(81.06, 2.44) * mm, "end": v(81.43, 3.31) * mm});
            skPoint(sketch, "E68.visualSharp", {"position": v(81.43, 4.55) * mm});
            skArc(sketch, "E68.filletArc", {"start": v(81.43, 3.31) * mm, "mid": v(81.06, 4.19) * mm, "end": v(80.19, 4.55) * mm});
            skPoint(sketch, "E69.visualSharp", {"position": v(95.28, 4.55) * mm});
            skArc(sketch, "E69.filletArc", {"start": v(95.28, 3.31) * mm, "mid": v(94.91, 4.19) * mm, "end": v(94.04, 4.55) * mm});
            skPoint(sketch, "E70.visualSharp", {"position": v(95.28, 2.07) * mm});
            skArc(sketch, "E70.filletArc", {"start": v(94.04, 2.07) * mm, "mid": v(94.91, 2.44) * mm, "end": v(95.28, 3.31) * mm});
            skPoint(sketch, "E71.visualSharp", {"position": v(82.18, 4.55) * mm});
            skArc(sketch, "E71.filletArc", {"start": v(83.42, 4.55) * mm, "mid": v(82.54, 4.19) * mm, "end": v(82.18, 3.31) * mm});
            skPoint(sketch, "E72.visualSharp", {"position": v(82.18, 2.07) * mm});
            skArc(sketch, "E72.filletArc", {"start": v(82.18, 3.31) * mm, "mid": v(82.54, 2.44) * mm, "end": v(83.42, 2.07) * mm});
            skPoint(sketch, "E73", {"position": v(76.12, 4.55) * mm});
            skPoint(sketch, "E74", {"position": v(88.73, 4.55) * mm});
            skPoint(sketch, "E75", {"position": v(99.89, 4.17) * mm});
            skLineSegment(sketch, "E76", {"start": v(99.89, 4.17) * mm, "end": v(105.5, 4.17) * mm});
            skSolve(sketch);
        }
        {
            var Q0;
            Q0=makeQuery(id+"F33.imprint","IMPRINT",FACE,{"disambiguationData":[TD([[makeQuery(id+"F33.imprint","IMPRINT",EDGE,{"derivedFrom":sQuery(id+"F33.wireOp",EDGE,"E64.bottom")}),1.0]])]});
            var Q1;
            Q1=makeQuery(id+"F33.imprint","IMPRINT",FACE,{"disambiguationData":[TD([[makeQuery(id+"F33.imprint","IMPRINT",EDGE,{"derivedFrom":sQuery(id+"F33.wireOp",EDGE,"E63.bottom")}),1.0]])]});
            extrude(context, id + "F34", {"entities" : qUnion([Q0, Q1]), "operationType" : NewBodyOperationType.ADD, "depth" : .4 * mm, "offsetDistance" : 25 * mm});
        }
        {
            var Q0;
            {var subQ0=sQuery(id+"F33.wireOp",EDGE,"E62.bottom");Q0=makeQuery(id+"F33.imprint","IMPRINT",FACE,{"disambiguationData":[TD([[makeQuery(id+"F33.imprint","IMPRINT",EDGE,{"derivedFrom":subQ0}),1.0]])]});}
            extrude(context, id + "F35", {"entities" : qUnion([Q0]), "depth" : .35 * mm, "offsetDistance" : 25 * mm});
        }
        {
            var Q0;
            Q0=sQuery(id+"F4.wireOp",EDGE,"E5.left");
            cPlane(context, id + "F36", {"entities" : qUnion([Q0]), "cplaneType" : CPlaneType.LINE_ANGLE, "offset" : 25 * mm, "angle" : 90 * degree, "width" : 150 * mm, "height" : 150 * mm});
        }
        {
            var Q0;
            Q0=qCreatedBy(id+"F36.planeOp",FACE);
            var sketch = newSketch(context, id + "F37", { "sketchPlane" : qUnion([Q0])});
            skLineSegment(sketch, "E77.bottom", {"start": v(92.8, 4.9) * mm, "end": v(84.66, 4.9) * mm});
            skLineSegment(sketch, "E77.top", {"start": v(92.8, 2.41) * mm, "end": v(84.66, 2.41) * mm});
            skLineSegment(sketch, "E77.left", {"start": v(83.42, 3.65) * mm, "end": v(83.42, 3.65) * mm});
            skLineSegment(sketch, "E77.right", {"start": v(94.04, 3.65) * mm, "end": v(94.04, 3.65) * mm});
            skPoint(sketch, "E78.firstSnap0", {"position": v(88.73, 4.9) * mm});
            skLineSegment(sketch, "E78.bottom", {"start": v(67.19, 4.9) * mm, "end": v(53.82, 4.89) * mm});
            skLineSegment(sketch, "E78.top", {"start": v(67.19, 2.45) * mm, "end": v(53.82, 2.45) * mm});
            skLineSegment(sketch, "E78.left", {"start": v(68.4, 3.67) * mm, "end": v(68.4, 3.67) * mm});
            skLineSegment(sketch, "E78.right", {"start": v(52.6, 3.67) * mm, "end": v(52.6, 3.67) * mm});
            skPoint(sketch, "E79", {"position": v(94.04, 3.65) * mm});
            skPoint(sketch, "E80.visualSharp", {"position": v(68.4, 4.9) * mm});
            skArc(sketch, "E80.filletArc", {"start": v(68.4, 3.67) * mm, "mid": v(68.05, 4.53) * mm, "end": v(67.19, 4.9) * mm});
            skPoint(sketch, "E81.visualSharp", {"position": v(68.4, 2.45) * mm});
            skArc(sketch, "E81.filletArc", {"start": v(67.19, 2.45) * mm, "mid": v(68.05, 2.8) * mm, "end": v(68.4, 3.67) * mm});
            skPoint(sketch, "E82.visualSharp", {"position": v(52.6, 2.45) * mm});
            skArc(sketch, "E82.filletArc", {"start": v(52.6, 3.67) * mm, "mid": v(52.95, 2.8) * mm, "end": v(53.82, 2.45) * mm});
            skPoint(sketch, "E83.visualSharp", {"position": v(52.6, 4.9) * mm});
            skArc(sketch, "E83.filletArc", {"start": v(53.82, 4.9) * mm, "mid": v(52.95, 4.53) * mm, "end": v(52.6, 3.67) * mm});
            skPoint(sketch, "E84.visualSharp", {"position": v(83.42, 4.9) * mm});
            skArc(sketch, "E84.filletArc", {"start": v(84.66, 4.9) * mm, "mid": v(83.78, 4.53) * mm, "end": v(83.42, 3.65) * mm});
            skPoint(sketch, "E85.visualSharp", {"position": v(83.42, 2.4) * mm});
            skArc(sketch, "E85.filletArc", {"start": v(83.42, 3.65) * mm, "mid": v(83.78, 2.77) * mm, "end": v(84.66, 2.41) * mm});
            skPoint(sketch, "E86.visualSharp", {"position": v(94.04, 2.41) * mm});
            skArc(sketch, "E86.filletArc", {"start": v(92.8, 2.41) * mm, "mid": v(93.67, 2.77) * mm, "end": v(94.04, 3.65) * mm});
            skPoint(sketch, "E87.visualSharp", {"position": v(94.04, 4.9) * mm});
            skArc(sketch, "E87.filletArc", {"start": v(94.04, 3.65) * mm, "mid": v(93.67, 4.53) * mm, "end": v(92.8, 4.9) * mm});
            skCircle(sketch, "E88", {"center": v(53.82, 3.67) * mm, "radius": 0.75 * mm});
            skSolve(sketch);
        }
        {
            var Q0;
            Q0=makeQuery(id+"F37.imprint","IMPRINT",FACE,{"disambiguationData":[TD([[makeQuery(id+"F37.imprint","IMPRINT",EDGE,{"derivedFrom":sQuery(id+"F37.wireOp",EDGE,"E78.bottom")}),1.0]])]});
            extrude(context, id + "F38", {"entities" : qUnion([Q0]), "operationType" : NewBodyOperationType.REMOVE, "depth" : .3 * mm, "offsetDistance" : 25 * mm});
        }
        {
            var Q0;
            Q0=makeQuery(id+"F37.imprint","IMPRINT",FACE,{"disambiguationData":[TD([[makeQuery(id+"F37.imprint","IMPRINT",EDGE,{"derivedFrom":sQuery(id+"F37.wireOp",EDGE,"E88")}),1.0]])]});
            extrude(context, id + "F39", {"entities" : qUnion([Q0]), "operationType" : NewBodyOperationType.REMOVE, "depth" : .5 * mm, "offsetDistance" : 25 * mm});
        }
        {
            var Q0;
            Q0=makeQuery(id+"F37.imprint","IMPRINT",FACE,{"disambiguationData":[TD([[makeQuery(id+"F37.imprint","IMPRINT",EDGE,{"derivedFrom":sQuery(id+"F37.wireOp",EDGE,"E77.bottom")}),1.0]])]});
            extrude(context, id + "F40", {"entities" : qUnion([Q0]), "operationType" : NewBodyOperationType.ADD, "depth" : .5 * mm, "offsetDistance" : 25 * mm});
        }
        {
            var Q0;
            {var subQ0=sQuery(id+"F33.wireOp",EDGE,"E62.bottom");Q0=makeQuery(id+"F33.imprint","IMPRINT",FACE,{"disambiguationData":[TD([[makeQuery(id+"F33.imprint","IMPRINT",EDGE,{"derivedFrom":subQ0}),1.0]])]});}
            extrude(context, id + "F41", {"entities" : qUnion([Q0]), "oppositeDirection" : true, "depth" : 3 * mm, "offsetDistance" : 25 * mm});
        }
        {
            var Q0;
            Q0=makeQuery(id+"F33.imprint","IMPRINT",FACE,{"disambiguationData":[TD([[makeQuery(id+"F33.imprint","IMPRINT",EDGE,{"derivedFrom":sQuery(id+"F33.wireOp",EDGE,"E63.bottom")}),1.0]])]});
            extrude(context, id + "F42", {"entities" : qUnion([Q0]), "operationType" : NewBodyOperationType.ADD, "oppositeDirection" : true, "depth" : 2 * mm, "offsetDistance" : 25 * mm});
        }
        {
            var Q0;
            Q0=makeQuery(id+"F33.imprint","IMPRINT",FACE,{"disambiguationData":[TD([[makeQuery(id+"F33.imprint","IMPRINT",EDGE,{"derivedFrom":sQuery(id+"F33.wireOp",EDGE,"E64.bottom")}),1.0]])]});
            extrude(context, id + "F43", {"entities" : qUnion([Q0]), "operationType" : NewBodyOperationType.ADD, "oppositeDirection" : true, "depth" : 25 * mm, "offsetDistance" : 25 * mm});
        }
        {
            var Q0;
            Q0=makeQuery(id+"F29.boolean.opBoolean","COPY",EDGE,{"derivedFrom":makeQuery(id+"F29.opExtrude","CAP_EDGE",EDGE,{"disambiguationData":[OSD([sQuery(id+"F23.wireOp",EDGE,"E53")])],"isStart":false})});
            fillet(context, id + "F44", {"entities" : qUnion([Q0]), "radius" : 21.71 * mm, "tangentPropagation" : true, "allowEdgeOverflow" : false});
        }
    });
